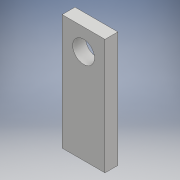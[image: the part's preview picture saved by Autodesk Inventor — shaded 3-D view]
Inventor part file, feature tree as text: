
AUTODESK INVENTOR PART (.ipt)
format: ipt  version: 2018 (Build 220112000, 112)  size: 225,280 bytes
history: native  units: mm
features: extrude x3, sketch x3
ambient origin geometry x8: Origin, YZ Plane, XZ Plane, XY Plane, X Axis, Y Axis, Z Axis, Center Point
bodies: Solid1 (feature_tree)
feature tree (6):
  extrude  "Extrusion1"  Depth=27.0mm
  extrude  "Extrusion2"  Depth=10.0mm
  extrude  "Extrusion4"  Depth=10.0mm TaperAngle=0.0deg
  sketch  "Sketch1"  dims[d0=10.0mm d1=27.0mm]
  sketch  "Sketch2"  dims[d2=10.0mm d3=0.0mm d4=5.0mm]
  sketch  "Sketch4"  dims[d5=5.1mm d6=10.0mm d7=0.0mm d13=27.0mm d14=7.0mm d15=0.0mm]
